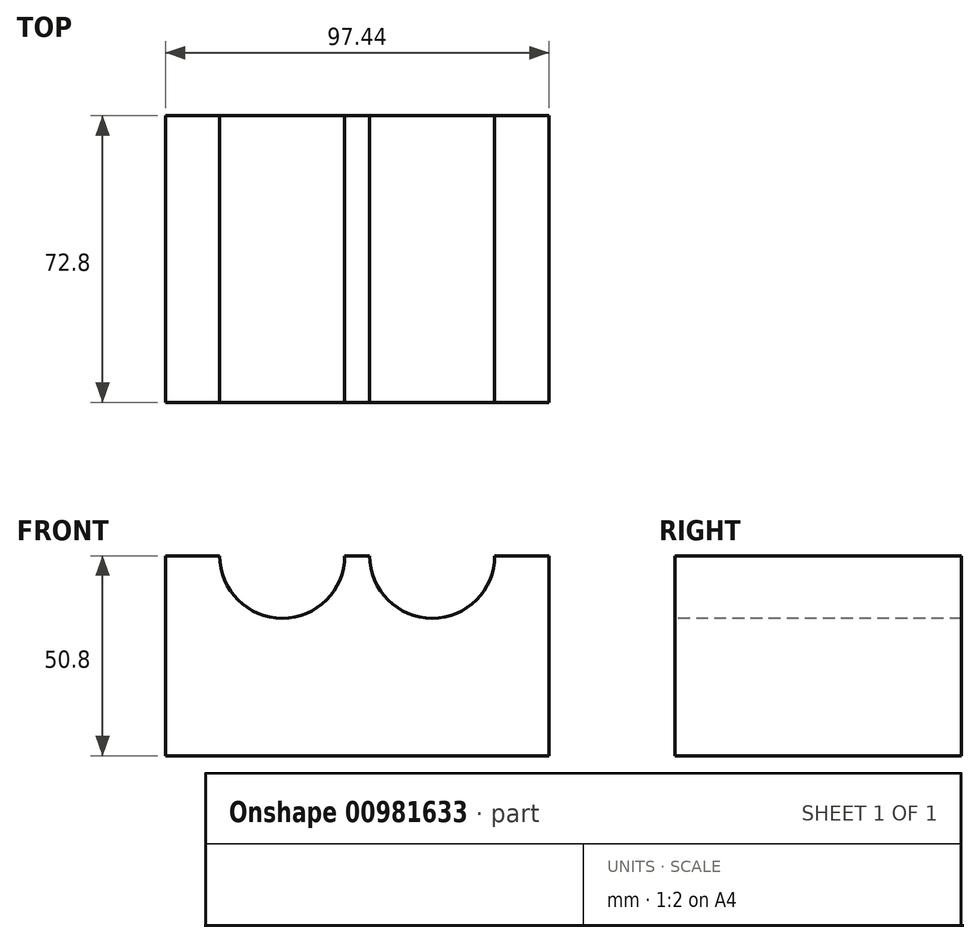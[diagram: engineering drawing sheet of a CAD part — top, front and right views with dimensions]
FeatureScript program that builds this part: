
annotation { "Feature Type Name" : "Feature", "Feature Type Description" : "" }
export const myFeature = defineFeature(function(context is Context, id is Id, definition is map)
    precondition{}
    {
        {
            var Q0;
            Q0=qCreatedBy(makeId("Top.planeOp"),FACE);
            var sketch = newSketch(context, id + "F0", { "sketchPlane" : qUnion([Q0])});
            skLineSegment(sketch, "E0.bottom", {"start": v(48.72, 36.4) * mm, "end": v(-48.72, 36.4) * mm});
            skLineSegment(sketch, "E0.top", {"start": v(48.72, -36.4) * mm, "end": v(-48.72, -36.4) * mm});
            skLineSegment(sketch, "E0.left", {"start": v(48.72, 36.4) * mm, "end": v(48.72, -36.4) * mm});
            skLineSegment(sketch, "E0.right", {"start": v(-48.72, 36.4) * mm, "end": v(-48.72, -36.4) * mm});
            skPoint(sketch, "E0.middle", {"position": v(0, 0) * mm});
            skSolve(sketch);
        }
        {
            var Q0;
            Q0 = qSketchRegion(id + "F0", true);
            extrude(context, id + "F1", {"entities" : qUnion([Q0]), "depth" : 50.8 * mm, "offsetDistance" : 25.4 * mm});
        }
        {
            var Q0;
            Q0=makeQuery(id+"F1.opExtrude","SWEPT_FACE",FACE,{"disambiguationData":[OSD([sQuery(id+"F0.wireOp",EDGE,"E0.top")])]});
            var sketch = newSketch(context, id + "F2", { "sketchPlane" : qUnion([Q0])});
            skCircle(sketch, "E1", {"center": v(-19.05, 50.8) * mm, "radius": 15.88 * mm});
            skCircle(sketch, "E2", {"center": v(19.05, 50.8) * mm, "radius": 15.88 * mm});
            skSolve(sketch);
        }
        {
            var Q0;
            Q0 = qSketchRegion(id + "F2", true);
            extrude(context, id + "F3", {"entities" : qUnion([Q0]), "operationType" : NewBodyOperationType.REMOVE, "endBound" : BoundingType.THROUGH_ALL, "oppositeDirection" : true, "depth" : 25.4 * mm, "offsetDistance" : 25.4 * mm});
        }
    });
